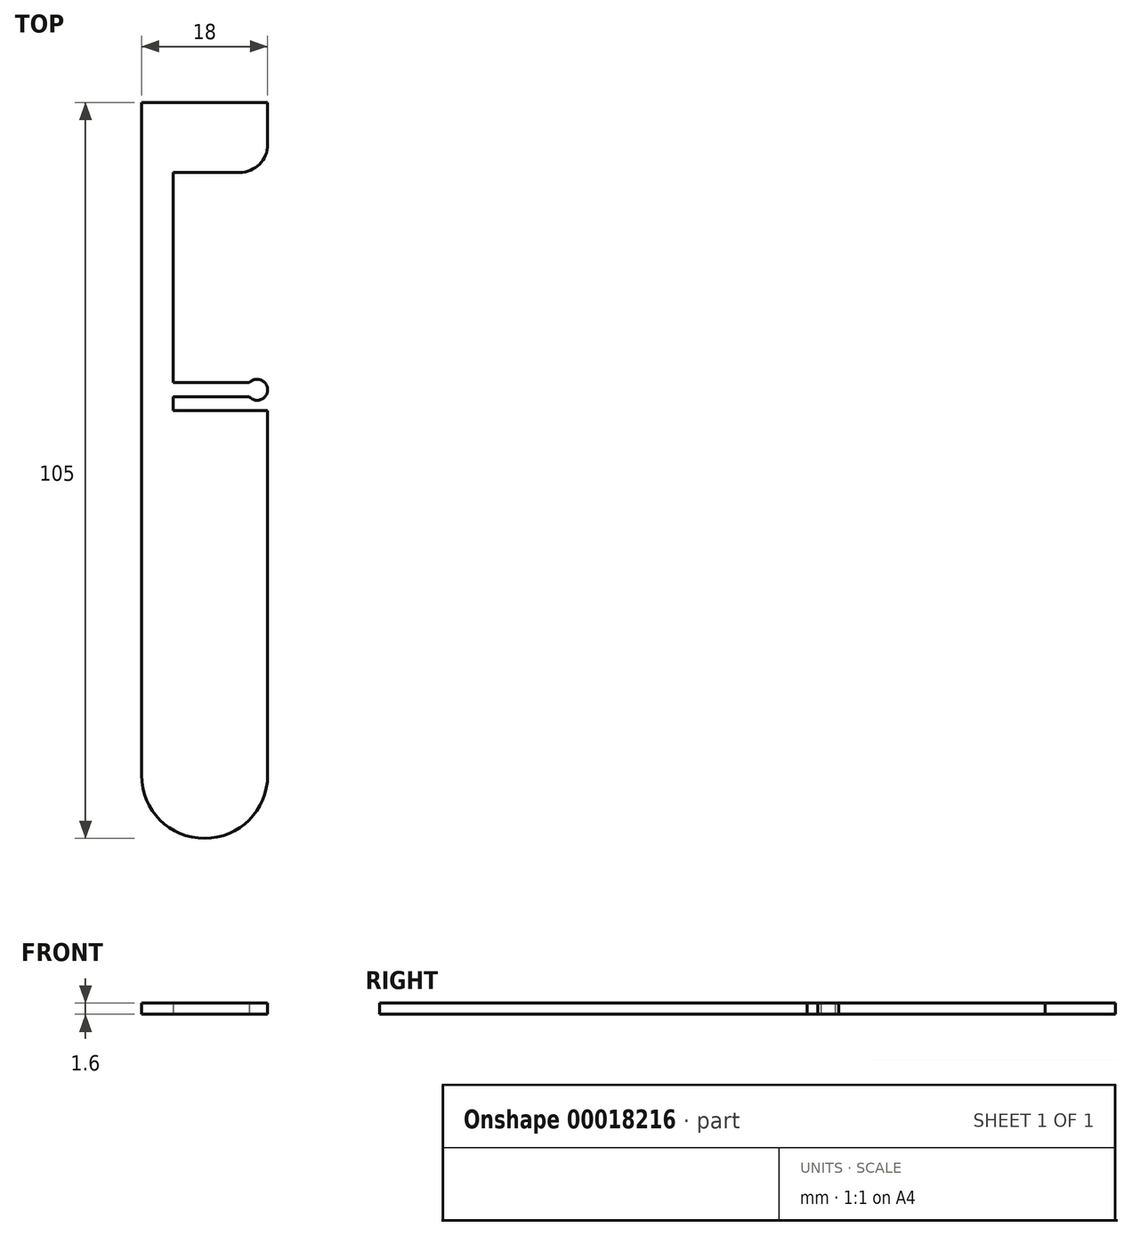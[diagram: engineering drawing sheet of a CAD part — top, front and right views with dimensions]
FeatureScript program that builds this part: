
annotation { "Feature Type Name" : "Feature", "Feature Type Description" : "" }
export const myFeature = defineFeature(function(context is Context, id is Id, definition is map)
    precondition{}
    {
        {
            var Q0;
            Q0=qCreatedBy(makeId("Top.planeOp"),FACE);
            var sketch = newSketch(context, id + "F0", { "sketchPlane" : qUnion([Q0])});
            skLineSegment(sketch, "E0", {"start": v(0, 0) * mm, "end": v(18, 0) * mm});
            skLineSegment(sketch, "E1", {"start": v(18, 0) * mm, "end": v(18, -6) * mm});
            skLineSegment(sketch, "E2", {"start": v(14, -10) * mm, "end": v(4.5, -10) * mm});
            skLineSegment(sketch, "E3", {"start": v(4.5, -10) * mm, "end": v(4.5, -40) * mm});
            skLineSegment(sketch, "E4", {"start": v(4.5, -40) * mm, "end": v(15.38, -40) * mm});
            skLineSegment(sketch, "E5", {"start": v(4.5, -42) * mm, "end": v(4.5, -44) * mm});
            skLineSegment(sketch, "E6", {"start": v(4.5, -44) * mm, "end": v(18, -44) * mm});
            skLineSegment(sketch, "E7", {"start": v(18, -44) * mm, "end": v(18, -96) * mm});
            skLineSegment(sketch, "E8", {"start": v(0, -96) * mm, "end": v(0, 0) * mm});
            skPoint(sketch, "E9.visualSharp", {"position": v(18, -10) * mm});
            skArc(sketch, "E9.filletArc", {"start": v(14, -10) * mm, "mid": v(16.83, -8.83) * mm, "end": v(18, -6) * mm});
            skArc(sketch, "E10", {"start": v(0, -96) * mm, "mid": v(9, -105) * mm, "end": v(18, -96) * mm});
            skArc(sketch, "E11", {"start": v(15.38, -42) * mm, "mid": v(18, -41) * mm, "end": v(15.38, -40) * mm});
            skLineSegment(sketch, "E12.trimOffspring", {"start": v(15.38, -42) * mm, "end": v(4.5, -42) * mm});
            skSolve(sketch);
        }
        {
            var Q0;
            Q0=makeQuery(id+"F0.imprint","IMPRINT",FACE,{"disambiguationData":[TD([[makeQuery(id+"F0.imprint","IMPRINT",EDGE,{"derivedFrom":sQuery(id+"F0.wireOp",EDGE,"E0")}),-1.0]])]});
            extrude(context, id + "F1", {"entities" : qUnion([Q0]), "depth" : 1.6 * mm});
        }
    });
